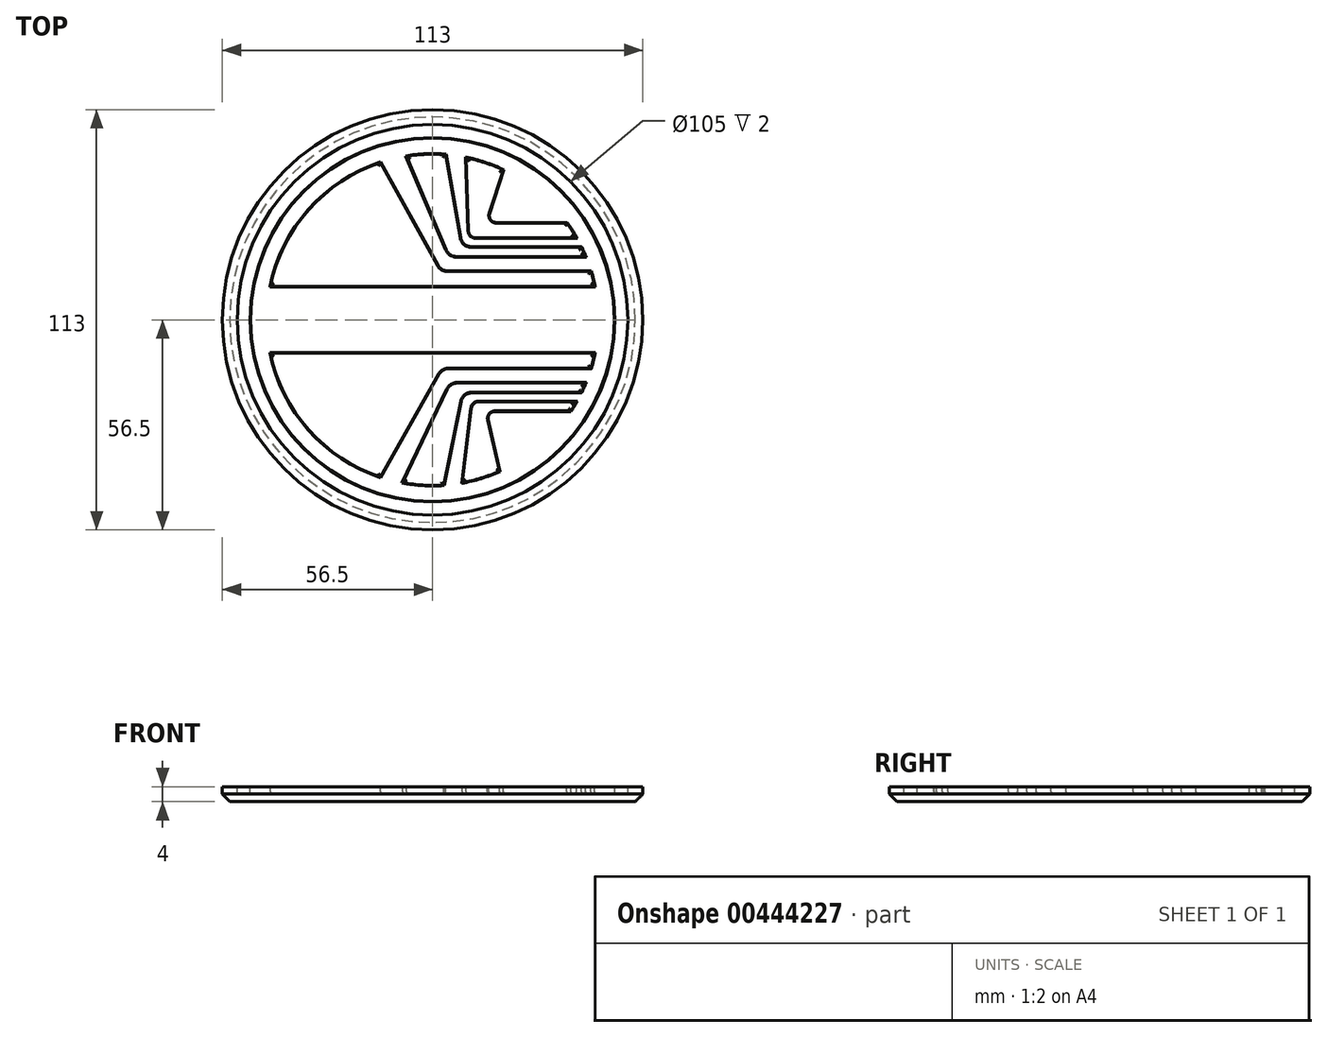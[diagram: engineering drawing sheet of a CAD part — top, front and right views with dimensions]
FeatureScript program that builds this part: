
annotation { "Feature Type Name" : "Feature", "Feature Type Description" : "" }
export const myFeature = defineFeature(function(context is Context, id is Id, definition is map)
    precondition{}
    {
        {
            var Q0;
            Q0=qCreatedBy(makeId("Top.planeOp"),FACE);
            var sketch = newSketch(context, id + "F0", { "sketchPlane" : qUnion([Q0])});
            skLineSegment(sketch, "E0", {"start": v(-61.02, 60) * mm, "end": v(61.02, -60) * mm, "construction": true});
            skSolve(sketch);
        }
        {
            var Q0;
            Q0=qCreatedBy(makeId("Top.planeOp"),FACE);
            var sketch = newSketch(context, id + "F1", { "sketchPlane" : qUnion([Q0])});
            skCircle(sketch, "E1", {"center": v(0, 0) * mm, "radius": 56.5 * mm});
            skCircle(sketch, "E2", {"center": v(0, 0) * mm, "radius": 52.5 * mm});
            skCircle(sketch, "E3", {"center": v(0, 0) * mm, "radius": 49 * mm});
            skLineSegment(sketch, "E4", {"start": v(-14, 42.24) * mm, "end": v(1.35, 14.55) * mm});
            skLineSegment(sketch, "E5", {"start": v(42.56, 13) * mm, "end": v(3.98, 13) * mm});
            skLineSegment(sketch, "E6", {"start": v(-7, 43.95) * mm, "end": v(3.66, 18.83) * mm});
            skLineSegment(sketch, "E7", {"start": v(6.42, 17) * mm, "end": v(41.12, 17) * mm});
            skLineSegment(sketch, "E8", {"start": v(3.5, 44.36) * mm, "end": v(7.45, 21.98) * mm});
            skLineSegment(sketch, "E9", {"start": v(10.4, 19.5) * mm, "end": v(40, 19.5) * mm});
            skLineSegment(sketch, "E10", {"start": v(9, 43.58) * mm, "end": v(9.69, 23.93) * mm});
            skLineSegment(sketch, "E11", {"start": v(11.68, 22) * mm, "end": v(38.68, 22) * mm});
            skLineSegment(sketch, "E12", {"start": v(19, 40.24) * mm, "end": v(15.22, 28.62) * mm});
            skLineSegment(sketch, "E13", {"start": v(17.13, 26) * mm, "end": v(36.11, 26) * mm});
            skPoint(sketch, "E14.visualSharp", {"position": v(2.2, 13) * mm});
            skArc(sketch, "E14.filletArc", {"start": v(1.35, 14.55) * mm, "mid": v(2.45, 13.42) * mm, "end": v(3.98, 13) * mm});
            skPoint(sketch, "E15.visualSharp", {"position": v(4.44, 17) * mm});
            skArc(sketch, "E15.filletArc", {"start": v(3.66, 18.83) * mm, "mid": v(4.77, 17.5) * mm, "end": v(6.42, 17) * mm});
            skPoint(sketch, "E16.visualSharp", {"position": v(7.88, 19.5) * mm});
            skArc(sketch, "E16.filletArc", {"start": v(7.45, 21.98) * mm, "mid": v(8.47, 20.2) * mm, "end": v(10.4, 19.5) * mm});
            skPoint(sketch, "E17.visualSharp", {"position": v(9.75, 22) * mm});
            skArc(sketch, "E17.filletArc", {"start": v(9.69, 23.93) * mm, "mid": v(10.3, 22.56) * mm, "end": v(11.68, 22) * mm});
            skPoint(sketch, "E18.visualSharp", {"position": v(14.37, 26) * mm});
            skArc(sketch, "E18.filletArc", {"start": v(15.22, 28.62) * mm, "mid": v(15.5, 26.82) * mm, "end": v(17.13, 26) * mm});
            skLineSegment(sketch, "E19", {"start": v(-43.58, 9) * mm, "end": v(43.58, 9) * mm});
            skLineSegment(sketch, "E20", {"start": v(-43.58, -9) * mm, "end": v(43.58, -9) * mm});
            skLineSegment(sketch, "E21", {"start": v(42.56, -13) * mm, "end": v(4.3, -13) * mm});
            skLineSegment(sketch, "E22", {"start": v(1.68, -14.52) * mm, "end": v(-14, -42.24) * mm});
            skLineSegment(sketch, "E23", {"start": v(41.12, -17) * mm, "end": v(6.66, -17) * mm});
            skLineSegment(sketch, "E24", {"start": v(3.96, -18.7) * mm, "end": v(-8, -43.77) * mm});
            skLineSegment(sketch, "E25", {"start": v(40, -19.5) * mm, "end": v(10.52, -19.5) * mm});
            skLineSegment(sketch, "E26", {"start": v(7.58, -21.9) * mm, "end": v(3, -44.4) * mm});
            skLineSegment(sketch, "E27", {"start": v(38.68, -22) * mm, "end": v(12.44, -22) * mm});
            skLineSegment(sketch, "E28", {"start": v(10.46, -23.76) * mm, "end": v(8, -43.77) * mm});
            skLineSegment(sketch, "E29", {"start": v(37.15, -24.5) * mm, "end": v(16.77, -24.5) * mm});
            skLineSegment(sketch, "E30", {"start": v(14.83, -26.95) * mm, "end": v(18, -40.7) * mm});
            skPoint(sketch, "E31.visualSharp", {"position": v(2.54, -13) * mm});
            skArc(sketch, "E31.filletArc", {"start": v(4.3, -13) * mm, "mid": v(2.78, -13.4) * mm, "end": v(1.68, -14.52) * mm});
            skPoint(sketch, "E32.visualSharp", {"position": v(4.77, -17) * mm});
            skArc(sketch, "E32.filletArc", {"start": v(6.66, -17) * mm, "mid": v(5.06, -17.46) * mm, "end": v(3.96, -18.7) * mm});
            skPoint(sketch, "E33.visualSharp", {"position": v(8.07, -19.5) * mm});
            skArc(sketch, "E33.filletArc", {"start": v(10.52, -19.5) * mm, "mid": v(8.62, -20.18) * mm, "end": v(7.58, -21.9) * mm});
            skPoint(sketch, "E34.visualSharp", {"position": v(10.67, -22) * mm});
            skArc(sketch, "E34.filletArc", {"start": v(12.44, -22) * mm, "mid": v(11.12, -22.5) * mm, "end": v(10.46, -23.76) * mm});
            skPoint(sketch, "E35.visualSharp", {"position": v(14.26, -24.5) * mm});
            skArc(sketch, "E35.filletArc", {"start": v(16.77, -24.5) * mm, "mid": v(15.2, -25.25) * mm, "end": v(14.83, -26.95) * mm});
            skArc(sketch, "E36", {"start": v(-43.58, 9) * mm, "mid": v(-44.5, 0) * mm, "end": v(-43.58, -9) * mm, "construction": true});
            skArc(sketch, "E37", {"start": v(-43.58, -9) * mm, "mid": v(-33.24, -29.58) * mm, "end": v(-14, -42.24) * mm});
            skArc(sketch, "E38", {"start": v(43.58, 9) * mm, "mid": v(43.12, 11.01) * mm, "end": v(42.56, 13) * mm});
            skArc(sketch, "E39", {"start": v(43.58, -9) * mm, "mid": v(44.5, 0) * mm, "end": v(43.58, 9) * mm, "construction": true});
            skArc(sketch, "E40", {"start": v(42.56, -13) * mm, "mid": v(43.12, -11.01) * mm, "end": v(43.58, -9) * mm});
            skArc(sketch, "E41", {"start": v(41.12, -17) * mm, "mid": v(41.89, -15.02) * mm, "end": v(42.56, -13) * mm, "construction": true});
            skArc(sketch, "E42", {"start": v(40, -19.5) * mm, "mid": v(40.58, -18.26) * mm, "end": v(41.12, -17) * mm});
            skArc(sketch, "E43", {"start": v(38.68, -22) * mm, "mid": v(39.36, -20.76) * mm, "end": v(40, -19.5) * mm, "construction": true});
            skArc(sketch, "E44", {"start": v(37.15, -24.5) * mm, "mid": v(37.94, -23.26) * mm, "end": v(38.68, -22) * mm});
            skArc(sketch, "E45", {"start": v(18, -40.7) * mm, "mid": v(28.74, -33.98) * mm, "end": v(37.15, -24.5) * mm, "construction": true});
            skArc(sketch, "E46", {"start": v(8, -43.77) * mm, "mid": v(13.1, -42.53) * mm, "end": v(18, -40.7) * mm});
            skArc(sketch, "E47", {"start": v(3, -44.4) * mm, "mid": v(5.5, -44.16) * mm, "end": v(8, -43.77) * mm, "construction": true});
            skArc(sketch, "E48", {"start": v(-8, -43.77) * mm, "mid": v(-2.52, -44.43) * mm, "end": v(3, -44.4) * mm});
            skArc(sketch, "E49", {"start": v(-14, -42.24) * mm, "mid": v(-11.03, -43.11) * mm, "end": v(-8, -43.77) * mm, "construction": true});
            skArc(sketch, "E50", {"start": v(-14, 42.24) * mm, "mid": v(-33.24, 29.58) * mm, "end": v(-43.58, 9) * mm});
            skArc(sketch, "E51", {"start": v(-7, 43.95) * mm, "mid": v(-10.53, 43.24) * mm, "end": v(-14, 42.24) * mm, "construction": true});
            skArc(sketch, "E52", {"start": v(3.5, 44.36) * mm, "mid": v(-1.76, 44.47) * mm, "end": v(-7, 43.95) * mm});
            skArc(sketch, "E53", {"start": v(9, 43.58) * mm, "mid": v(6.26, 44.06) * mm, "end": v(3.5, 44.36) * mm, "construction": true});
            skArc(sketch, "E54", {"start": v(19, 40.24) * mm, "mid": v(14.1, 42.2) * mm, "end": v(9, 43.58) * mm});
            skArc(sketch, "E55", {"start": v(36.11, 26) * mm, "mid": v(28.46, 34.2) * mm, "end": v(19, 40.24) * mm, "construction": true});
            skArc(sketch, "E56", {"start": v(38.68, 22) * mm, "mid": v(37.45, 24.03) * mm, "end": v(36.11, 26) * mm});
            skArc(sketch, "E57", {"start": v(40, 19.5) * mm, "mid": v(39.36, 20.76) * mm, "end": v(38.68, 22) * mm, "construction": true});
            skArc(sketch, "E58", {"start": v(41.12, 17) * mm, "mid": v(40.58, 18.26) * mm, "end": v(40, 19.5) * mm});
            skArc(sketch, "E59", {"start": v(42.56, 13) * mm, "mid": v(41.89, 15.02) * mm, "end": v(41.12, 17) * mm, "construction": true});
            skSolve(sketch);
        }
        {
            var Q0;
            Q0=makeQuery(id+"F1.imprint","IMPRINT",FACE,{"disambiguationData":[TD([[makeQuery(id+"F1.imprint","IMPRINT",EDGE,{"derivedFrom":sQuery(id+"F1.wireOp",EDGE,"E1")}),1.0]])]});
            var Q1;
            Q1=makeQuery(id+"F1.imprint","IMPRINT",FACE,{"disambiguationData":[TD([[makeQuery(id+"F1.imprint","IMPRINT",EDGE,{"derivedFrom":sQuery(id+"F1.wireOp",EDGE,"E2")}),1.0]])]});
            var Q2;
            Q2=makeQuery(id+"F1.imprint","IMPRINT",FACE,{"disambiguationData":[TD([[makeQuery(id+"F1.imprint","IMPRINT",EDGE,{"derivedFrom":sQuery(id+"F1.wireOp",EDGE,"E3")}),1.0]])]});
            var Q3;
            Q3=makeQuery(id+"F1.imprint","IMPRINT",FACE,{"disambiguationData":[TD([[makeQuery(id+"F1.imprint","IMPRINT",EDGE,{"derivedFrom":sQuery(id+"F1.wireOp",EDGE,"E23")}),1.0]])]});
            var Q4;
            Q4=makeQuery(id+"F1.imprint","IMPRINT",FACE,{"disambiguationData":[TD([[makeQuery(id+"F1.imprint","IMPRINT",EDGE,{"derivedFrom":sQuery(id+"F1.wireOp",EDGE,"E27")}),1.0]])]});
            var Q5;
            Q5=makeQuery(id+"F1.imprint","IMPRINT",FACE,{"disambiguationData":[TD([[makeQuery(id+"F1.imprint","IMPRINT",EDGE,{"derivedFrom":sQuery(id+"F1.wireOp",EDGE,"E4")}),-1.0]])]});
            var Q6;
            Q6=makeQuery(id+"F1.imprint","IMPRINT",FACE,{"disambiguationData":[TD([[makeQuery(id+"F1.imprint","IMPRINT",EDGE,{"derivedFrom":sQuery(id+"F1.wireOp",EDGE,"E6")}),1.0]])]});
            var Q7;
            Q7=makeQuery(id+"F1.imprint","IMPRINT",FACE,{"disambiguationData":[TD([[makeQuery(id+"F1.imprint","IMPRINT",EDGE,{"derivedFrom":sQuery(id+"F1.wireOp",EDGE,"E10")}),1.0]])]});
            var Q8;
            Q8=makeQuery(id+"F1.imprint","IMPRINT",FACE,{"disambiguationData":[TD([[makeQuery(id+"F1.imprint","IMPRINT",EDGE,{"derivedFrom":sQuery(id+"F1.wireOp",EDGE,"E20")}),-1.0]])]});
            extrude(context, id + "F2", {"entities" : qUnion([Q0, Q1, Q2, Q3, Q4, Q5, Q6, Q7, Q8]), "oppositeDirection" : true, "depth" : 4 * mm});
        }
        {
            var Q0;
            Q0=makeQuery(id+"F1.imprint","IMPRINT",FACE,{"disambiguationData":[TD([[makeQuery(id+"F1.imprint","IMPRINT",EDGE,{"derivedFrom":sQuery(id+"F1.wireOp",EDGE,"E2")}),1.0]])]});
            var Q1;
            Q1=makeQuery(id+"F1.imprint","IMPRINT",FACE,{"disambiguationData":[TD([[makeQuery(id+"F1.imprint","IMPRINT",EDGE,{"derivedFrom":sQuery(id+"F1.wireOp",EDGE,"E4")}),-1.0]])]});
            var Q2;
            Q2=makeQuery(id+"F1.imprint","IMPRINT",FACE,{"disambiguationData":[TD([[makeQuery(id+"F1.imprint","IMPRINT",EDGE,{"derivedFrom":sQuery(id+"F1.wireOp",EDGE,"E6")}),1.0]])]});
            var Q3;
            Q3=makeQuery(id+"F1.imprint","IMPRINT",FACE,{"disambiguationData":[TD([[makeQuery(id+"F1.imprint","IMPRINT",EDGE,{"derivedFrom":sQuery(id+"F1.wireOp",EDGE,"E10")}),1.0]])]});
            var Q4;
            Q4=makeQuery(id+"F1.imprint","IMPRINT",FACE,{"disambiguationData":[TD([[makeQuery(id+"F1.imprint","IMPRINT",EDGE,{"derivedFrom":sQuery(id+"F1.wireOp",EDGE,"E27")}),1.0]])]});
            var Q5;
            Q5=makeQuery(id+"F1.imprint","IMPRINT",FACE,{"disambiguationData":[TD([[makeQuery(id+"F1.imprint","IMPRINT",EDGE,{"derivedFrom":sQuery(id+"F1.wireOp",EDGE,"E23")}),1.0]])]});
            var Q6;
            Q6=makeQuery(id+"F1.imprint","IMPRINT",FACE,{"disambiguationData":[TD([[makeQuery(id+"F1.imprint","IMPRINT",EDGE,{"derivedFrom":sQuery(id+"F1.wireOp",EDGE,"E20")}),-1.0]])]});
            extrude(context, id + "F3", {"entities" : qUnion([Q0, Q1, Q2, Q3, Q4, Q5, Q6]), "operationType" : NewBodyOperationType.REMOVE, "oppositeDirection" : true, "depth" : 2 * mm});
        }
        {
            var Q0;
            Q0=makeQuery(id+"F3.boolean.opBoolean","COPY",FACE,{"derivedFrom":makeQuery(id+"F3.opExtrude","CAP_FACE",FACE,{"disambiguationData":[OSD([sQuery(id+"F1.wireOp",EDGE,"E4"),sQuery(id+"F1.wireOp",EDGE,"E5"),sQuery(id+"F1.wireOp",EDGE,"E14.filletArc"),sQuery(id+"F1.wireOp",EDGE,"E19"),sQuery(id+"F1.wireOp",EDGE,"E38"),sQuery(id+"F1.wireOp",EDGE,"E50")])],"isStart":false})});
            var Q1;
            Q1=makeQuery(id+"F3.boolean.opBoolean","COPY",FACE,{"derivedFrom":makeQuery(id+"F3.opExtrude","CAP_FACE",FACE,{"disambiguationData":[OSD([sQuery(id+"F1.wireOp",EDGE,"E6"),sQuery(id+"F1.wireOp",EDGE,"E7"),sQuery(id+"F1.wireOp",EDGE,"E8"),sQuery(id+"F1.wireOp",EDGE,"E9"),sQuery(id+"F1.wireOp",EDGE,"E15.filletArc"),sQuery(id+"F1.wireOp",EDGE,"E16.filletArc"),sQuery(id+"F1.wireOp",EDGE,"E52"),sQuery(id+"F1.wireOp",EDGE,"E58")])],"isStart":false})});
            var Q2;
            Q2=makeQuery(id+"F3.boolean.opBoolean","COPY",FACE,{"derivedFrom":makeQuery(id+"F3.opExtrude","CAP_FACE",FACE,{"disambiguationData":[OSD([sQuery(id+"F1.wireOp",EDGE,"E10"),sQuery(id+"F1.wireOp",EDGE,"E11"),sQuery(id+"F1.wireOp",EDGE,"E12"),sQuery(id+"F1.wireOp",EDGE,"E13"),sQuery(id+"F1.wireOp",EDGE,"E17.filletArc"),sQuery(id+"F1.wireOp",EDGE,"E18.filletArc"),sQuery(id+"F1.wireOp",EDGE,"E54"),sQuery(id+"F1.wireOp",EDGE,"E56")])],"isStart":false})});
            var Q3;
            Q3=makeQuery(id+"F3.boolean.opBoolean","COPY",FACE,{"derivedFrom":makeQuery(id+"F3.opExtrude","CAP_FACE",FACE,{"disambiguationData":[OSD([sQuery(id+"F1.wireOp",EDGE,"E20"),sQuery(id+"F1.wireOp",EDGE,"E21"),sQuery(id+"F1.wireOp",EDGE,"E22"),sQuery(id+"F1.wireOp",EDGE,"E31.filletArc"),sQuery(id+"F1.wireOp",EDGE,"E37"),sQuery(id+"F1.wireOp",EDGE,"E40")])],"isStart":false})});
            var Q4;
            Q4=makeQuery(id+"F3.boolean.opBoolean","COPY",FACE,{"derivedFrom":makeQuery(id+"F3.opExtrude","CAP_FACE",FACE,{"disambiguationData":[OSD([sQuery(id+"F1.wireOp",EDGE,"E23"),sQuery(id+"F1.wireOp",EDGE,"E24"),sQuery(id+"F1.wireOp",EDGE,"E25"),sQuery(id+"F1.wireOp",EDGE,"E26"),sQuery(id+"F1.wireOp",EDGE,"E32.filletArc"),sQuery(id+"F1.wireOp",EDGE,"E33.filletArc"),sQuery(id+"F1.wireOp",EDGE,"E42"),sQuery(id+"F1.wireOp",EDGE,"E48")])],"isStart":false})});
            var Q5;
            Q5=makeQuery(id+"F3.boolean.opBoolean","COPY",FACE,{"derivedFrom":makeQuery(id+"F3.opExtrude","CAP_FACE",FACE,{"disambiguationData":[OSD([sQuery(id+"F1.wireOp",EDGE,"E27"),sQuery(id+"F1.wireOp",EDGE,"E28"),sQuery(id+"F1.wireOp",EDGE,"E29"),sQuery(id+"F1.wireOp",EDGE,"E30"),sQuery(id+"F1.wireOp",EDGE,"E34.filletArc"),sQuery(id+"F1.wireOp",EDGE,"E35.filletArc"),sQuery(id+"F1.wireOp",EDGE,"E44"),sQuery(id+"F1.wireOp",EDGE,"E46")])],"isStart":false})});
            fillet(context, id + "F4", {"entities" : qUnion([Q0, Q1, Q2, Q3, Q4, Q5]), "radius" : .75 * mm, "tangentPropagation" : true, "allowEdgeOverflow" : false});
        }
        {
            var Q0;
            Q0=makeQuery(id+"F3.boolean.opBoolean","SPLIT",FACE,{"disambiguationData":[TD([makeQuery(id+"F3.opExtrude","SWEPT_FACE",FACE,{"disambiguationData":[OSD([sQuery(id+"F1.wireOp",EDGE,"E3")])]})])],"derivedFrom":makeQuery(id+"F2.opExtrude","CAP_FACE",FACE,{"disambiguationData":[OSD([sQuery(id+"F1.wireOp",EDGE,"E1")])],"isStart":true})});
            chamfer(context, id + "F5", {"entities" : qUnion([Q0]), "width" : .15 * mm, "tangentPropagation" : true});
        }
        {
            var Q0;
            Q0=makeQuery(id+"F2.opExtrude","CAP_EDGE",EDGE,{"disambiguationData":[OSD([sQuery(id+"F1.wireOp",EDGE,"E1")])],"isStart":false});
            chamfer(context, id + "F6", {"entities" : qUnion([Q0]), "width" : 2 * mm, "tangentPropagation" : true});
        }
    });
